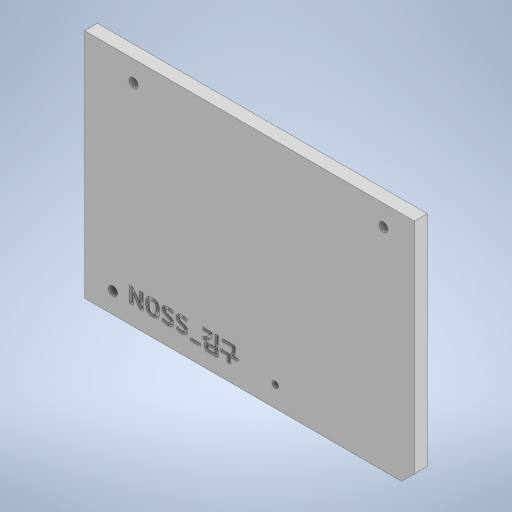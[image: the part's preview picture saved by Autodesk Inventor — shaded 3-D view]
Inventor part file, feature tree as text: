
AUTODESK INVENTOR PART (.ipt)
format: ipt  version: 2023 (Build 270158000, 158)  size: 386,560 bytes
history: native  units: mm
features: extrude x2, sketch x2, other x1
ambient origin geometry x8: Origin, YZ Plane, XZ Plane, XY Plane, X Axis, Y Axis, Z Axis, Center Point
bodies: Body1 (feature_tree)
feature tree (5):
  other  "솔리드1"
  extrude  "돌출1"  Depth=128.0mm
  extrude  "돌출2"  Depth=90.0mm
  sketch  "스케치1"
  sketch  "스케치2"
